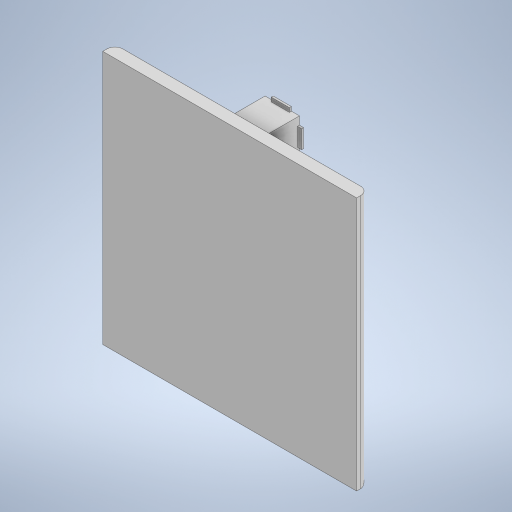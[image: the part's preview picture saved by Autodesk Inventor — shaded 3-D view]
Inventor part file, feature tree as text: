
AUTODESK INVENTOR PART (.ipt)
format: ipt  version: 2024 (Build 280153000, 153)  size: 257,024 bytes
history: native  units: mm
features: extrude x3, sketch x3, fillet x1
ambient origin geometry x8: Origin, YZ Plane, XZ Plane, XY Plane, X Axis, Y Axis, Z Axis, Center Point
bodies: Volumenkörper1 (feature_tree)
feature tree (7):
  extrude  "Extrusion1"  Depth=62.7mm
  extrude  "Extrusion2"  Depth=2.5mm
  extrude  "Extrusion3"  Depth=2.0mm
  fillet  "Rundung1"  Radius=4.25mm
  sketch  "Skizze1"  dims[d0=62.7mm d1=62.7mm]
  sketch  "Skizze2"  dims[d2=3.0mm d3=0.0mm d6=2.5mm]
  sketch  "Skizze3"  dims[d7=8.5mm d9=4.25mm d10=4.25mm d11=10.0mm d12=0.0mm d16=0.5mm d17=0.0mm d18=1.0mm d19=1.0mm d21=1.0mm d22=1.0mm d23=2.0mm d24=2.0mm d25=2.0mm d26=2.0mm d27=2.0mm d28=2.0mm d29=2.0mm d30=2.0mm]
